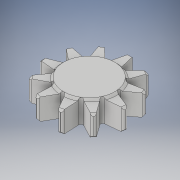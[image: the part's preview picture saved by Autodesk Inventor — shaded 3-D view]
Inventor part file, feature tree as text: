
AUTODESK INVENTOR PART (.ipt)
format: ipt  version: 2019 (Build 230136000, 136)  size: 306,176 bytes
history: native  units: mm
features: sketch x2, other x1, extrude x1, pattern_circular x1
ambient origin geometry x8: Origin, YZ Plane, XZ Plane, XY Plane, X Axis, Y Axis, Z Axis, Center Point
bodies: Solide1 (feature_tree)
feature tree (5):
  other  "Révolution1"
  extrude  "Extrusion1"  Depth=5.0mm
  pattern_circular  "Réseau circulaire1"  [2 undecoded]
  sketch  "Esquisse1"
  sketch  "Esquisse2"
note: 2 required parameter values undecoded (feature->parameter linkage not recoverable at this tier; creation-order binding heuristic only, values carry confidence <= 0.55)
